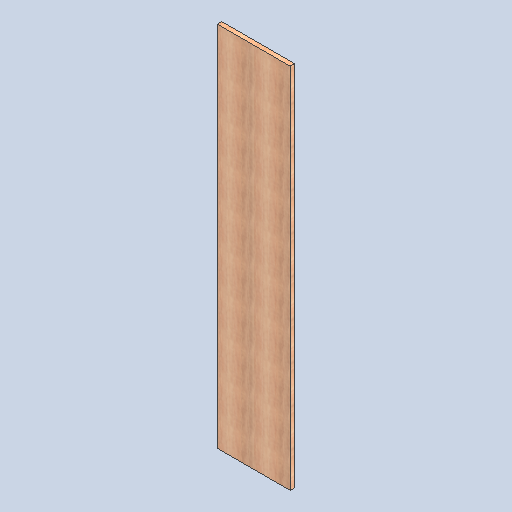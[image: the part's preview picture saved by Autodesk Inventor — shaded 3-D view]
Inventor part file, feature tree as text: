
AUTODESK INVENTOR PART (.ipt)
format: ipt  version: 2025 (Build 290162000, 162)  size: 156,672 bytes
history: native  units: mm
features: extrude x1
ambient origin geometry x8: Origin, YZ Plane, XZ Plane, XY Plane, X Axis, Y Axis, Z Axis, Center Point
bodies: Solid1 (feature_tree)
feature tree (1):
  extrude  "Extrusion1"  Depth=494.0mm
